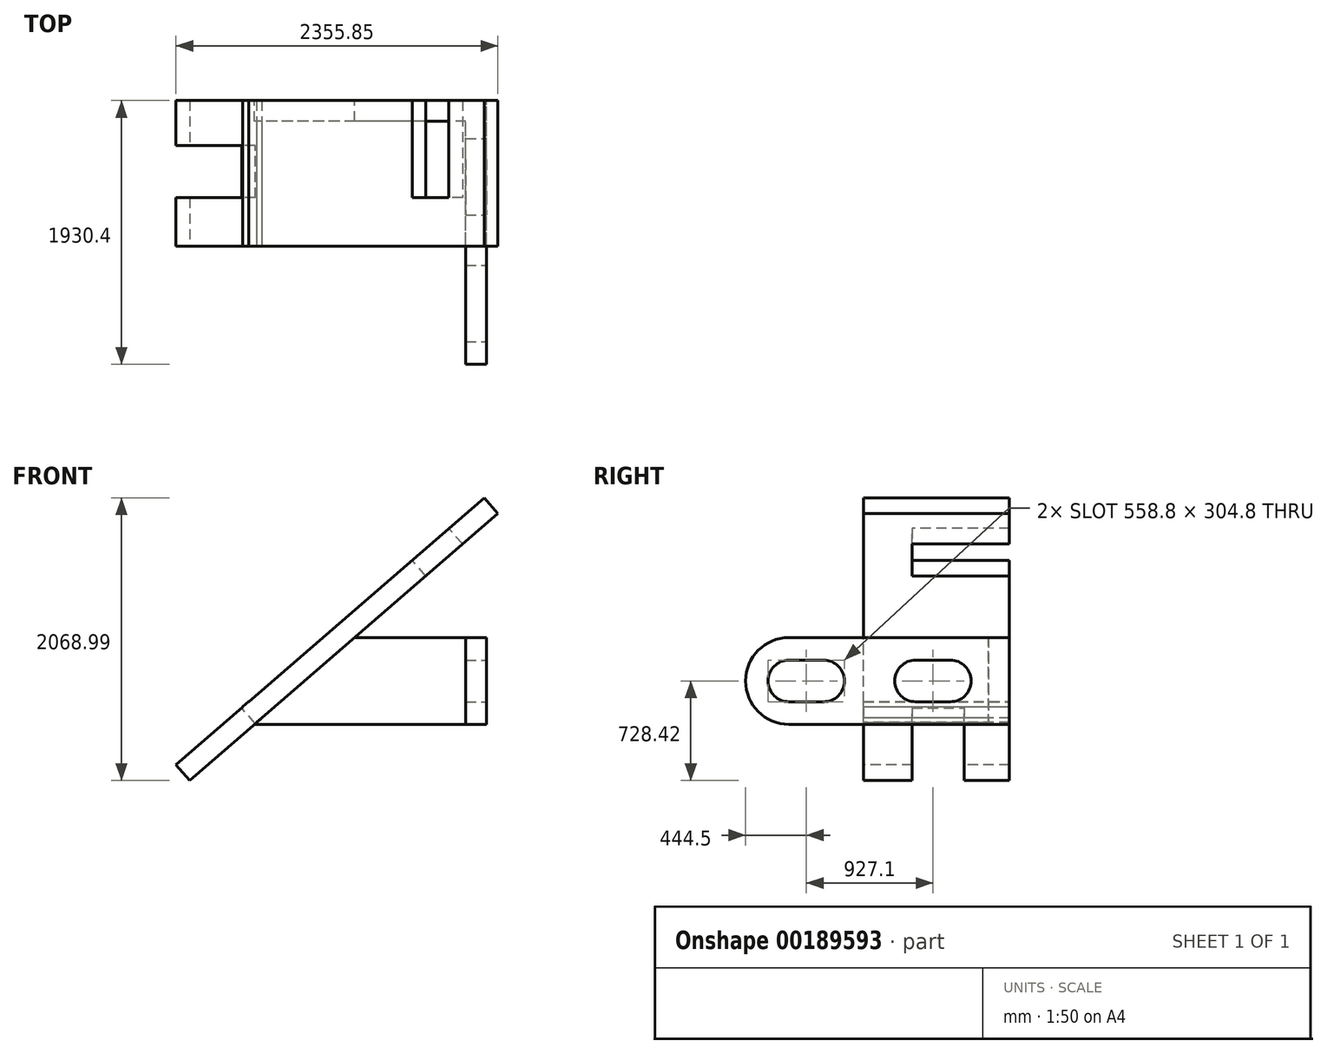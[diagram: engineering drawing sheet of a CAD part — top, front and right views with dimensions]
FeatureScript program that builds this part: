
annotation { "Feature Type Name" : "Feature", "Feature Type Description" : "" }
export const myFeature = defineFeature(function(context is Context, id is Id, definition is map)
    precondition{}
    {
        {
            var Q0;
            Q0=qCreatedBy(makeId("Right.planeOp"),FACE);
            var sketch = newSketch(context, id + "F0", { "sketchPlane" : qUnion([Q0])});
            skLineSegment(sketch, "E0.bottom", {"start": v(0, 0) * mm, "end": v(-1612.9, 0) * mm});
            skLineSegment(sketch, "E0.top", {"start": v(0, 609.6) * mm, "end": v(-1612.9, 609.6) * mm});
            skLineSegment(sketch, "E0.left", {"start": v(0, 0) * mm, "end": v(0, 609.6) * mm});
            skLineSegment(sketch, "E0.right", {"start": v(-1612.9, 0) * mm, "end": v(-1612.9, 609.6) * mm});
            skLineSegment(sketch, "E1.bottom", {"start": v(-1612.9, 609.6) * mm, "end": v(0, 609.6) * mm});
            skLineSegment(sketch, "E1.top", {"start": v(-1612.9, 622.3) * mm, "end": v(0, 622.3) * mm});
            skLineSegment(sketch, "E1.left", {"start": v(-1612.9, 609.6) * mm, "end": v(-1612.9, 622.3) * mm});
            skLineSegment(sketch, "E1.right", {"start": v(0, 609.6) * mm, "end": v(0, 622.3) * mm});
            skLineSegment(sketch, "E2.bottom", {"start": v(-1612.9, 0) * mm, "end": v(0, 0) * mm});
            skLineSegment(sketch, "E2.top", {"start": v(-1612.9, -12.7) * mm, "end": v(0, -12.7) * mm});
            skLineSegment(sketch, "E2.left", {"start": v(-1612.9, 0) * mm, "end": v(-1612.9, -12.7) * mm});
            skLineSegment(sketch, "E2.right", {"start": v(0, 0) * mm, "end": v(0, -12.7) * mm});
            skSolve(sketch);
        }
        {
            var Q0;
            Q0 = qSketchRegion(id + "F0", true);
            extrude(context, id + "F1", {"entities" : qUnion([Q0]), "oppositeDirection" : true, "depth" : 152.4 * mm});
        }
        {
            var Q0;
            Q0=makeQuery(id+"F1.opExtrude","CAP_FACE",FACE,{"disambiguationData":[OSD([sQuery(id+"F0.wireOp",EDGE,"E0.bottom"),sQuery(id+"F0.wireOp",EDGE,"E0.top"),sQuery(id+"F0.wireOp",EDGE,"E0.left"),sQuery(id+"F0.wireOp",EDGE,"E0.right")])],"isStart":true});
            var sketch = newSketch(context, id + "F2", { "sketchPlane" : qUnion([Q0])});
            skLineSegment(sketch, "E3", {"start": v(0, 609.6) * mm, "end": v(0, 457.2) * mm, "construction": true});
            skLineSegment(sketch, "E4", {"start": v(0, 457.2) * mm, "end": v(0, 152.4) * mm, "construction": true});
            skLineSegment(sketch, "E5", {"start": v(0, 457.2) * mm, "end": v(-431.8, 457.2) * mm, "construction": true});
            skLineSegment(sketch, "E6.bottom", {"start": v(-431.8, 457.2) * mm, "end": v(-685.8, 457.2) * mm});
            skLineSegment(sketch, "E6.top", {"start": v(-431.8, 152.4) * mm, "end": v(-685.8, 152.4) * mm});
            skLineSegment(sketch, "E6.left", {"start": v(-431.8, 457.2) * mm, "end": v(-431.8, 152.4) * mm});
            skLineSegment(sketch, "E6.right", {"start": v(-685.8, 457.2) * mm, "end": v(-685.8, 152.4) * mm});
            skLineSegment(sketch, "E7", {"start": v(-685.8, 457.2) * mm, "end": v(-1358.9, 457.2) * mm, "construction": true});
            skLineSegment(sketch, "E8.bottom", {"start": v(-1358.9, 457.2) * mm, "end": v(-1612.9, 457.2) * mm});
            skLineSegment(sketch, "E8.top", {"start": v(-1358.9, 152.4) * mm, "end": v(-1612.9, 152.4) * mm});
            skLineSegment(sketch, "E8.left", {"start": v(-1358.9, 457.2) * mm, "end": v(-1358.9, 152.4) * mm});
            skLineSegment(sketch, "E8.right", {"start": v(-1612.9, 457.2) * mm, "end": v(-1612.9, 152.4) * mm});
            skSolve(sketch);
        }
        {
            var Q0;
            Q0 = qSketchRegion(id + "F2", true);
            extrude(context, id + "F3", {"entities" : qUnion([Q0]), "operationType" : NewBodyOperationType.REMOVE, "oppositeDirection" : true, "depth" : 152.4 * mm});
        }
        {
            var Q0;
            Q0=makeQuery(id+"F1.opExtrude","CAP_FACE",FACE,{"disambiguationData":[OSD([sQuery(id+"F0.wireOp",EDGE,"E0.bottom"),sQuery(id+"F0.wireOp",EDGE,"E0.top"),sQuery(id+"F0.wireOp",EDGE,"E0.left"),sQuery(id+"F0.wireOp",EDGE,"E0.right")])],"isStart":true});
            var sketch = newSketch(context, id + "F4", { "sketchPlane" : qUnion([Q0])});
            skLineSegment(sketch, "E9.bottom", {"start": v(-1612.9, 622.3) * mm, "end": v(-1930.4, 622.3) * mm});
            skLineSegment(sketch, "E9.top", {"start": v(-1612.9, -12.7) * mm, "end": v(-1930.4, -12.7) * mm});
            skLineSegment(sketch, "E9.left", {"start": v(-1612.9, 622.3) * mm, "end": v(-1612.9, -12.7) * mm});
            skLineSegment(sketch, "E9.right", {"start": v(-1930.4, 622.3) * mm, "end": v(-1930.4, -12.7) * mm});
            skSolve(sketch);
        }
        {
            var Q0;
            Q0 = qSketchRegion(id + "F4", true);
            extrude(context, id + "F5", {"entities" : qUnion([Q0]), "operationType" : NewBodyOperationType.ADD, "oppositeDirection" : true, "depth" : 152.4 * mm});
        }
        {
            var Q0;
            Q0=makeQuery(id+"F5.opExtrude","SWEPT_EDGE",EDGE,{"disambiguationData":[OSD([sQuery(id+"F4.wireOp",EDGE,"u6ZnYJE4-glCc-nvjx-bhtg-3rpyIsKAPTDI.bottom"),sQuery(id+"F4.wireOp",EDGE,"u6ZnYJE4-glCc-nvjx-bhtg-3rpyIsKAPTDI.right")])]});
            var Q1;
            Q1=makeQuery(id+"F5.opExtrude","SWEPT_EDGE",EDGE,{"disambiguationData":[OSD([sQuery(id+"F4.wireOp",EDGE,"u6ZnYJE4-glCc-nvjx-bhtg-3rpyIsKAPTDI.top"),sQuery(id+"F4.wireOp",EDGE,"u6ZnYJE4-glCc-nvjx-bhtg-3rpyIsKAPTDI.right")])]});
            var Q2;
            Q2=makeQuery(id+"F5.opExtrude","SWEPT_EDGE",EDGE,{"disambiguationData":[OSD([sQuery(id+"F4.wireOp",EDGE,"E9.bottom"),sQuery(id+"F4.wireOp",EDGE,"E9.right")])]});
            var Q3;
            Q3=makeQuery(id+"F5.opExtrude","SWEPT_EDGE",EDGE,{"disambiguationData":[OSD([sQuery(id+"F4.wireOp",EDGE,"E9.top"),sQuery(id+"F4.wireOp",EDGE,"E9.right")])]});
            fillet(context, id + "F6", {"entities" : qUnion([Q0, Q1, Q2, Q3]), "radius" : 317.5 * mm, "tangentPropagation" : true, "allowEdgeOverflow" : false});
        }
        {
            var Q0;
            Q0=makeQuery(id+"F5.boolean.opBoolean","MERGE",FACE,{"derivedFrom":[makeQuery(id+"F1.opExtrude","CAP_FACE",FACE,{"disambiguationData":[OSD([sQuery(id+"F0.wireOp",EDGE,"E0.bottom"),sQuery(id+"F0.wireOp",EDGE,"E0.top"),sQuery(id+"F0.wireOp",EDGE,"E0.left"),sQuery(id+"F0.wireOp",EDGE,"E0.right")])],"isStart":true}),makeQuery(id+"F5.opExtrude","CAP_FACE",FACE,{"disambiguationData":[OSD([sQuery(id+"F4.wireOp",EDGE,"u6ZnYJE4-glCc-nvjx-bhtg-3rpyIsKAPTDI.bottom"),sQuery(id+"F4.wireOp",EDGE,"u6ZnYJE4-glCc-nvjx-bhtg-3rpyIsKAPTDI.top"),sQuery(id+"F4.wireOp",EDGE,"u6ZnYJE4-glCc-nvjx-bhtg-3rpyIsKAPTDI.left"),sQuery(id+"F4.wireOp",EDGE,"u6ZnYJE4-glCc-nvjx-bhtg-3rpyIsKAPTDI.right")])],"isStart":true})]});
            var sketch = newSketch(context, id + "F7", { "sketchPlane" : qUnion([Q0])});
            skPoint(sketch, "E10", {"position": v(-1358.9, 304.8) * mm});
            skPoint(sketch, "E11", {"position": v(-685.8, 304.8) * mm});
            skPoint(sketch, "E12", {"position": v(-431.8, 304.8) * mm});
            skPoint(sketch, "E13", {"position": v(-1612.9, 304.8) * mm});
            skCircle(sketch, "E14", {"center": v(-1612.9, 304.8) * mm, "radius": 152.4 * mm});
            skCircle(sketch, "E15", {"center": v(-1358.9, 304.8) * mm, "radius": 152.4 * mm});
            skCircle(sketch, "E16", {"center": v(-685.8, 304.8) * mm, "radius": 152.4 * mm});
            skCircle(sketch, "E17", {"center": v(-431.8, 304.8) * mm, "radius": 152.4 * mm});
            skSolve(sketch);
        }
        {
            var Q0;
            Q0 = qSketchRegion(id + "F7", true);
            extrude(context, id + "F8", {"entities" : qUnion([Q0]), "operationType" : NewBodyOperationType.REMOVE, "oppositeDirection" : true, "depth" : 152.4 * mm});
        }
        {
            var Q0;
            Q0=makeQuery(id+"F1.opExtrude","SWEPT_FACE",FACE,{"disambiguationData":[OSD([sQuery(id+"F0.wireOp",EDGE,"E0.left"),sQuery(id+"F0.wireOp",EDGE,"E1.right"),sQuery(id+"F0.wireOp",EDGE,"E2.right")])]});
            var sketch = newSketch(context, id + "F9", { "sketchPlane" : qUnion([Q0])});
            skLineSegment(sketch, "E18.bottom", {"start": v(0, 622.3) * mm, "end": v(965.2, 622.3) * mm});
            skLineSegment(sketch, "E18.top", {"start": v(0, -12.7) * mm, "end": v(965.2, -12.7) * mm});
            skLineSegment(sketch, "E18.left", {"start": v(0, 622.3) * mm, "end": v(0, -12.7) * mm});
            skLineSegment(sketch, "E18.right", {"start": v(965.2, 622.3) * mm, "end": v(965.2, -12.7) * mm});
            skSolve(sketch);
        }
        {
            var Q0;
            Q0 = qSketchRegion(id + "F9", true);
            extrude(context, id + "F10", {"entities" : qUnion([Q0]), "operationType" : NewBodyOperationType.ADD, "oppositeDirection" : true, "depth" : 152.4 * mm});
        }
        {
            var Q0;
            Q0=makeQuery(id+"F10.boolean.opBoolean","MERGE",FACE,{"derivedFrom":[makeQuery(id+"F1.opExtrude","SWEPT_FACE",FACE,{"disambiguationData":[OSD([sQuery(id+"F0.wireOp",EDGE,"E0.left"),sQuery(id+"F0.wireOp",EDGE,"E1.right"),sQuery(id+"F0.wireOp",EDGE,"E2.right")])]}),makeQuery(id+"F10.opExtrude","CAP_FACE",FACE,{"disambiguationData":[OSD([sQuery(id+"F9.wireOp",EDGE,"E18.bottom"),sQuery(id+"F9.wireOp",EDGE,"E18.top"),sQuery(id+"F9.wireOp",EDGE,"E18.left"),sQuery(id+"F9.wireOp",EDGE,"E18.right")])],"isStart":true})]});
            var sketch = newSketch(context, id + "F11", { "sketchPlane" : qUnion([Q0])});
            skLineSegment(sketch, "E19", {"start": v(965.2, 622.3) * mm, "end": v(1698.45, -12.7) * mm});
            skLineSegment(sketch, "E20", {"start": v(1698.45, -12.7) * mm, "end": v(965.2, -12.7) * mm});
            skLineSegment(sketch, "E21", {"start": v(965.2, -12.7) * mm, "end": v(965.2, 622.3) * mm});
            skSolve(sketch);
        }
        {
            var Q0;
            Q0 = qSketchRegion(id + "F11", true);
            extrude(context, id + "F12", {"entities" : qUnion([Q0]), "operationType" : NewBodyOperationType.ADD, "oppositeDirection" : true, "depth" : 152.4 * mm});
        }
        {
            var Q0;
            Q0=makeQuery(id+"F12.opExtrude","SWEPT_FACE",FACE,{"disambiguationData":[OSD([sQuery(id+"F11.wireOp",EDGE,"E19")])]});
            cPlane(context, id + "F13", {"entities" : qUnion([Q0]), "cplaneType" : CPlaneType.OFFSET, "offset" : 0 * mm, "width" : 152.4 * mm, "height" : 152.4 * mm});
        }
        {
            var Q0;
            Q0=qCreatedBy(id+"F13.planeOp",FACE);
            var sketch = newSketch(context, id + "F14", { "sketchPlane" : qUnion([Q0])});
            skPoint(sketch, "E22", {"position": v(-1874.68, -395) * mm});
            skLineSegment(sketch, "E23.bottom", {"start": v(-1272.23, 0) * mm, "end": v(-1919.93, 0) * mm});
            skLineSegment(sketch, "E23.top", {"start": v(-1272.23, -1066.8) * mm, "end": v(-1919.93, -1066.8) * mm});
            skLineSegment(sketch, "E23.left", {"start": v(-1272.23, 0) * mm, "end": v(-1272.23, -1066.8) * mm});
            skLineSegment(sketch, "E23.right", {"start": v(-1919.93, 0) * mm, "end": v(-1919.93, -1066.8) * mm});
            skSolve(sketch);
        }
        {
            var Q0;
            Q0 = qSketchRegion(id + "F14", true);
            extrude(context, id + "F15", {"entities" : qUnion([Q0]), "operationType" : NewBodyOperationType.ADD, "depth" : 152.4 * mm});
        }
        {
            var Q0;
            Q0=qCreatedBy(id+"F13.planeOp",FACE);
            var sketch = newSketch(context, id + "F16", { "sketchPlane" : qUnion([Q0])});
            skLineSegment(sketch, "E24.bottom", {"start": v(-1222.3, 0) * mm, "end": v(1114.5, 0) * mm});
            skLineSegment(sketch, "E24.top", {"start": v(-1222.3, -1066.8) * mm, "end": v(1114.5, -1066.8) * mm});
            skLineSegment(sketch, "E24.left", {"start": v(-1222.3, 0) * mm, "end": v(-1222.3, -1066.8) * mm});
            skLineSegment(sketch, "E24.right", {"start": v(1114.5, 0) * mm, "end": v(1114.5, -1066.8) * mm});
            skSolve(sketch);
        }
        {
            var Q0;
            Q0=makeQuery(id+"F16.imprint","IMPRINT",FACE,{"disambiguationData":[TD([[makeQuery(id+"F16.imprint","IMPRINT",EDGE,{"derivedFrom":sQuery(id+"F16.wireOp",EDGE,"E24.bottom")}),-1.0]])]});
            extrude(context, id + "F17", {"entities" : qUnion([Q0]), "operationType" : NewBodyOperationType.ADD, "depth" : 152.4 * mm});
        }
        {
            var Q0;
            {var subQ0=sQuery(id+"F16.wireOp",EDGE,"E24.bottom");var subQ1=sQuery(id+"F14.wireOp",EDGE,"E23.bottom");var subQ2=sQuery(id+"F11.wireOp",EDGE,"E20");var subQ3=sQuery(id+"F9.wireOp",EDGE,"E18.top");var subQ4=sQuery(id+"F9.wireOp",EDGE,"E18.bottom");var subQ5=sQuery(id+"F0.wireOp",EDGE,"E2.right");var subQ6=sQuery(id+"F0.wireOp",EDGE,"E1.right");var subQ7=sQuery(id+"F0.wireOp",EDGE,"E0.left");Q0=makeQuery(id+"FdpdoXQGTB0HgMN_1.boolean.opBoolean","MERGE",FACE,{"derivedFrom":[makeQuery(id+"F17.boolean.opBoolean","MERGE",FACE,{"derivedFrom":[makeQuery(id+"F15.boolean.opBoolean","MERGE",FACE,{"derivedFrom":[makeQuery(id+"F12.boolean.opBoolean","MERGE",FACE,{"derivedFrom":[makeQuery(id+"F10.boolean.opBoolean","MERGE",FACE,{"derivedFrom":[makeQuery(id+"F1.opExtrude","SWEPT_FACE",FACE,{"disambiguationData":[OSD([subQ7,subQ6,subQ5])]}),makeQuery(id+"F10.opExtrude","CAP_FACE",FACE,{"disambiguationData":[OSD([subQ4,subQ3,sQuery(id+"F9.wireOp",EDGE,"E18.left"),sQuery(id+"F9.wireOp",EDGE,"E18.right")])],"isStart":true})]}),makeQuery(id+"F12.opExtrude","CAP_FACE",FACE,{"disambiguationData":[OSD([sQuery(id+"F11.wireOp",EDGE,"E19"),subQ2,sQuery(id+"F11.wireOp",EDGE,"E21")])],"isStart":true})]}),makeQuery(id+"F15.opExtrude","SWEPT_FACE",FACE,{"disambiguationData":[OSD([subQ1])]})]}),makeQuery(id+"F17.opExtrude","SWEPT_FACE",FACE,{"disambiguationData":[OSD([subQ0])]})]}),makeQuery(id+"FdpdoXQGTB0HgMN_1.opExtrude","CAP_FACE",FACE,{"disambiguationData":[OSD([subQ7,sQuery(id+"F0.wireOp",EDGE,"E1.top"),subQ6,sQuery(id+"F0.wireOp",EDGE,"E2.top"),subQ5,subQ4,subQ3,subQ2,subQ1,sQuery(id+"F14.wireOp",EDGE,"E23.right"),subQ0,sQuery(id+"F16.wireOp",EDGE,"E24.right"),sQuery(id+"F3JF0fcBN3KHXI6_1.wireOp",EDGE,"93EAGQcv-1aPX-TRvg-ekPX-QmrGLh00WwtS")])],"isStart":true})]});}
            var sketch = newSketch(context, id + "F18", { "sketchPlane" : qUnion([Q0])});
            skLineSegment(sketch, "E25", {"start": v(-21.12, 1678.06) * mm, "end": v(16.63, 1645.37) * mm});
            skLineSegment(sketch, "E26", {"start": v(16.63, 1645.37) * mm, "end": v(-83.14, 1530.17) * mm});
            skLineSegment(sketch, "E27", {"start": v(-83.14, 1530.17) * mm, "end": v(-120.88, 1562.86) * mm});
            skLineSegment(sketch, "E28", {"start": v(-120.88, 1562.86) * mm, "end": v(-21.12, 1678.06) * mm});
            skSolve(sketch);
        }
        {
            var Q0;
            Q0 = qSketchRegion(id + "F18", true);
            extrude(context, id + "F19", {"entities" : qUnion([Q0]), "operationType" : NewBodyOperationType.REMOVE, "oppositeDirection" : true, "depth" : 1066.8 * mm});
        }
        {
            var Q0;
            Q0=makeQuery(id+"F17.boolean.opBoolean","MERGE",FACE,{"derivedFrom":[makeQuery(id+"F15.boolean.opBoolean","MERGE",FACE,{"derivedFrom":[makeQuery(id+"F12.boolean.opBoolean","MERGE",FACE,{"derivedFrom":[makeQuery(id+"F10.boolean.opBoolean","MERGE",FACE,{"derivedFrom":[makeQuery(id+"F1.opExtrude","SWEPT_FACE",FACE,{"disambiguationData":[OSD([sQuery(id+"F0.wireOp",EDGE,"E0.left"),sQuery(id+"F0.wireOp",EDGE,"E1.right"),sQuery(id+"F0.wireOp",EDGE,"E2.right")])]}),makeQuery(id+"F10.opExtrude","CAP_FACE",FACE,{"disambiguationData":[OSD([sQuery(id+"F9.wireOp",EDGE,"E18.bottom"),sQuery(id+"F9.wireOp",EDGE,"E18.top"),sQuery(id+"F9.wireOp",EDGE,"E18.left"),sQuery(id+"F9.wireOp",EDGE,"E18.right")])],"isStart":true})]}),makeQuery(id+"F12.opExtrude","CAP_FACE",FACE,{"disambiguationData":[OSD([sQuery(id+"F11.wireOp",EDGE,"E19"),sQuery(id+"F11.wireOp",EDGE,"E20"),sQuery(id+"F11.wireOp",EDGE,"E21")])],"isStart":true})]}),makeQuery(id+"F15.opExtrude","SWEPT_FACE",FACE,{"disambiguationData":[OSD([sQuery(id+"F14.wireOp",EDGE,"E23.bottom")])]})]}),makeQuery(id+"F17.opExtrude","SWEPT_FACE",FACE,{"disambiguationData":[OSD([sQuery(id+"F16.wireOp",EDGE,"E24.bottom")])]})]});
            cPlane(context, id + "F20", {"entities" : qUnion([Q0]), "cplaneType" : CPlaneType.OFFSET, "offset" : 0 * mm, "width" : 152.4 * mm, "height" : 152.4 * mm});
        }
        {
            var Q0;
            Q0=qCreatedBy(id+"F20.planeOp",FACE);
            var sketch = newSketch(context, id + "F21", { "sketchPlane" : qUnion([Q0])});
            skLineSegment(sketch, "E29", {"start": v(1684.72, 0) * mm, "end": v(1640.56, 38.24) * mm});
            skLineSegment(sketch, "E30", {"start": v(1684.72, 0) * mm, "end": v(1784.5, 115.2) * mm});
            skLineSegment(sketch, "E31", {"start": v(1784.5, 115.2) * mm, "end": v(1740.33, 153.45) * mm});
            skLineSegment(sketch, "E32", {"start": v(1740.33, 153.45) * mm, "end": v(1640.56, 38.24) * mm});
            skSolve(sketch);
        }
        {
            var Q0;
            Q0 = qSketchRegion(id + "F21", true);
            extrude(context, id + "F22", {"entities" : qUnion([Q0]), "operationType" : NewBodyOperationType.ADD, "oppositeDirection" : true, "depth" : 1066.8 * mm});
        }
        {
            var Q0;
            Q0=makeQuery(id+"F15.opExtrude","CAP_FACE",FACE,{"disambiguationData":[OSD([sQuery(id+"F14.wireOp",EDGE,"E23.bottom"),sQuery(id+"F14.wireOp",EDGE,"E23.top"),sQuery(id+"F14.wireOp",EDGE,"E23.left"),sQuery(id+"F14.wireOp",EDGE,"E23.right")])],"isStart":false});
            var sketch = newSketch(context, id + "F23", { "sketchPlane" : qUnion([Q0])});
            skLineSegment(sketch, "E33.bottom", {"start": v(-1919.93, -1066.8) * mm, "end": v(-1284.93, -1066.8) * mm, "construction": true});
            skLineSegment(sketch, "E33.top", {"start": v(-1919.93, -711.2) * mm, "end": v(-1284.93, -711.2) * mm, "construction": true});
            skLineSegment(sketch, "E33.left", {"start": v(-1919.93, -1066.8) * mm, "end": v(-1919.93, -711.2) * mm, "construction": true});
            skLineSegment(sketch, "E33.right", {"start": v(-1284.93, -1066.8) * mm, "end": v(-1284.93, -711.2) * mm, "construction": true});
            skLineSegment(sketch, "E34.bottom", {"start": v(-1284.93, -711.2) * mm, "end": v(-1919.93, -711.2) * mm});
            skLineSegment(sketch, "E34.top", {"start": v(-1284.93, -330.2) * mm, "end": v(-1919.93, -330.2) * mm});
            skLineSegment(sketch, "E34.left", {"start": v(-1284.93, -711.2) * mm, "end": v(-1284.93, -330.2) * mm});
            skLineSegment(sketch, "E34.right", {"start": v(-1919.93, -711.2) * mm, "end": v(-1919.93, -330.2) * mm});
            skSolve(sketch);
        }
        {
            var Q0;
            Q0 = qSketchRegion(id + "F23", true);
            extrude(context, id + "F24", {"entities" : qUnion([Q0]), "operationType" : NewBodyOperationType.REMOVE, "oppositeDirection" : true, "depth" : 152.4 * mm});
        }
        {
            var Q0;
            Q0=makeQuery(id+"F17.opExtrude","CAP_FACE",FACE,{"disambiguationData":[OSD([sQuery(id+"F16.wireOp",EDGE,"E24.bottom"),sQuery(id+"F16.wireOp",EDGE,"E24.top"),sQuery(id+"F16.wireOp",EDGE,"E24.left"),sQuery(id+"F16.wireOp",EDGE,"E24.right")])],"isStart":false});
            var sketch = newSketch(context, id + "F25", { "sketchPlane" : qUnion([Q0])});
            skLineSegment(sketch, "E35.bottom", {"start": v(1064.57, 0) * mm, "end": v(721.67, 0) * mm, "construction": true});
            skLineSegment(sketch, "E35.top", {"start": v(1064.57, -711.2) * mm, "end": v(721.67, -711.2) * mm, "construction": true});
            skLineSegment(sketch, "E35.left", {"start": v(1064.57, 0) * mm, "end": v(1064.57, -711.2) * mm, "construction": true});
            skLineSegment(sketch, "E35.right", {"start": v(721.67, 0) * mm, "end": v(721.67, -711.2) * mm, "construction": true});
            skLineSegment(sketch, "E36.bottom", {"start": v(721.67, 0) * mm, "end": v(366.07, 0) * mm});
            skLineSegment(sketch, "E36.top", {"start": v(721.67, -711.2) * mm, "end": v(366.07, -711.2) * mm});
            skLineSegment(sketch, "E36.left", {"start": v(721.67, 0) * mm, "end": v(721.67, -711.2) * mm});
            skLineSegment(sketch, "E36.right", {"start": v(366.07, 0) * mm, "end": v(366.07, -711.2) * mm});
            skSolve(sketch);
        }
        {
            var Q0;
            Q0 = qSketchRegion(id + "F25", true);
            extrude(context, id + "F26", {"entities" : qUnion([Q0]), "operationType" : NewBodyOperationType.REMOVE, "oppositeDirection" : true, "depth" : 152.4 * mm});
        }
    });
